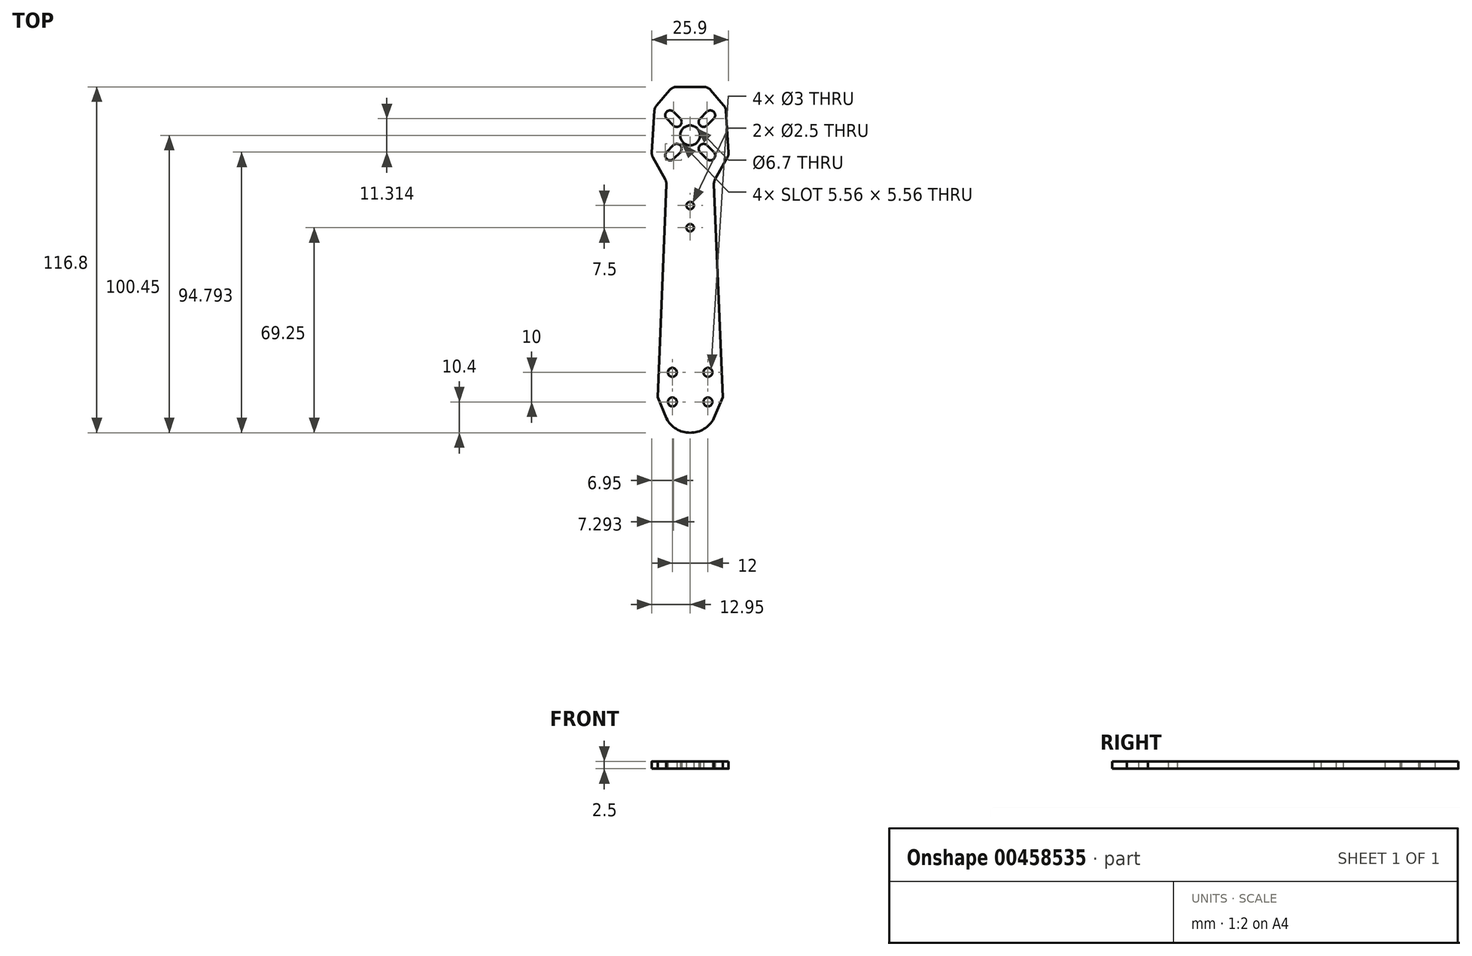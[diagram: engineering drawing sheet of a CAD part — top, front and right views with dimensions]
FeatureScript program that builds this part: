
annotation { "Feature Type Name" : "Feature", "Feature Type Description" : "" }
export const myFeature = defineFeature(function(context is Context, id is Id, definition is map)
    precondition{}
    {
        {
            var Q0;
            Q0=qCreatedBy(makeId("Top.planeOp"),FACE);
            var sketch = newSketch(context, id + "F0", { "sketchPlane" : qUnion([Q0])});
            skLineSegment(sketch, "E0", {"start": v(-11, -56) * mm, "end": v(-8.03, 15.96) * mm});
            skLineSegment(sketch, "E1", {"start": v(-8.4, 17.54) * mm, "end": v(-12.57, 25.03) * mm});
            skLineSegment(sketch, "E2", {"start": v(-12.95, 26.68) * mm, "end": v(-12.06, 40.8) * mm});
            skLineSegment(sketch, "E3", {"start": v(-11.35, 42.56) * mm, "end": v(-6.9, 47.75) * mm});
            skLineSegment(sketch, "E4", {"start": v(-4.62, 48.8) * mm, "end": v(4.62, 48.8) * mm});
            skLineSegment(sketch, "E5", {"start": v(6.9, 47.75) * mm, "end": v(11.35, 42.56) * mm});
            skLineSegment(sketch, "E6", {"start": v(12.06, 40.8) * mm, "end": v(12.95, 26.68) * mm});
            skLineSegment(sketch, "E7", {"start": v(12.57, 25.03) * mm, "end": v(8.4, 17.54) * mm});
            skLineSegment(sketch, "E8", {"start": v(8.03, 15.96) * mm, "end": v(11, -56) * mm});
            skLineSegment(sketch, "E9", {"start": v(11, -56) * mm, "end": v(8, -63.13) * mm});
            skLineSegment(sketch, "E10", {"start": v(-8, -63.13) * mm, "end": v(-11, -56) * mm});
            skPoint(sketch, "E11.visualSharp", {"position": v(0, -68) * mm});
            skArc(sketch, "E12", {"start": v(-8, -63.13) * mm, "mid": v(0, -68) * mm, "end": v(8, -63.13) * mm});
            skCircle(sketch, "E13", {"center": v(6, -47.6) * mm, "radius": 1.5 * mm});
            skCircle(sketch, "E14", {"center": v(-6, -47.6) * mm, "radius": 1.5 * mm});
            skCircle(sketch, "E15", {"center": v(6, -57.6) * mm, "radius": 1.5 * mm});
            skCircle(sketch, "E16", {"center": v(-6, -57.6) * mm, "radius": 1.5 * mm});
            skLineSegment(sketch, "E17", {"start": v(0, -68) * mm, "end": v(9.63, -68) * mm, "construction": true});
            skCircle(sketch, "E18", {"center": v(0, 1.25) * mm, "radius": 1.25 * mm});
            skCircle(sketch, "E19", {"center": v(0, 8.75) * mm, "radius": 1.25 * mm});
            skCircle(sketch, "E20", {"center": v(0, 32.45) * mm, "radius": 3.35 * mm});
            skPoint(sketch, "E20.centerSnap0", {"position": v(0, 48.8) * mm});
            skLineSegment(sketch, "E21", {"start": v(0, 32.45) * mm, "end": v(4.53, 27.92) * mm, "construction": true});
            skLineSegment(sketch, "E22", {"start": v(0, 32.45) * mm, "end": v(4.53, 36.98) * mm, "construction": true});
            skLineSegment(sketch, "E23", {"start": v(4.53, 36.98) * mm, "end": v(6.79, 39.24) * mm});
            skArc(sketch, "E24.0.startCap", {"start": v(5.7, 35.8) * mm, "mid": v(3.36, 35.8) * mm, "end": v(3.36, 38.14) * mm});
            skArc(sketch, "E24.0.endCap", {"start": v(5.62, 40.4) * mm, "mid": v(7.95, 40.4) * mm, "end": v(7.95, 38.07) * mm});
            skLineSegment(sketch, "E24.0.left", {"start": v(3.36, 38.14) * mm, "end": v(5.62, 40.4) * mm});
            skLineSegment(sketch, "E24.0.right", {"start": v(5.7, 35.8) * mm, "end": v(7.95, 38.07) * mm});
            skLineSegment(sketch, "E25.MirrorCS", {"start": v(-4.53, 36.98) * mm, "end": v(-6.79, 39.24) * mm});
            skLineSegment(sketch, "E26.MirrorCS", {"start": v(-4.53, 27.92) * mm, "end": v(-6.79, 25.66) * mm});
            skLineSegment(sketch, "E27.MirrorCS", {"start": v(4.53, 27.92) * mm, "end": v(6.79, 25.66) * mm});
            skArc(sketch, "E28.0.startCap", {"start": v(-3.36, 38.14) * mm, "mid": v(-3.36, 35.8) * mm, "end": v(-5.7, 35.8) * mm});
            skArc(sketch, "E28.0.endCap", {"start": v(-7.95, 38.07) * mm, "mid": v(-7.95, 40.4) * mm, "end": v(-5.62, 40.4) * mm});
            skLineSegment(sketch, "E28.0.left", {"start": v(-5.7, 35.8) * mm, "end": v(-7.95, 38.07) * mm});
            skLineSegment(sketch, "E28.0.right", {"start": v(-3.36, 38.14) * mm, "end": v(-5.62, 40.4) * mm});
            skArc(sketch, "E29.0.startCap", {"start": v(3.36, 26.76) * mm, "mid": v(3.36, 29.1) * mm, "end": v(5.7, 29.1) * mm});
            skArc(sketch, "E29.0.endCap", {"start": v(7.95, 26.83) * mm, "mid": v(7.95, 24.5) * mm, "end": v(5.62, 24.5) * mm});
            skLineSegment(sketch, "E29.0.left", {"start": v(5.7, 29.1) * mm, "end": v(7.95, 26.83) * mm});
            skLineSegment(sketch, "E29.0.right", {"start": v(3.36, 26.76) * mm, "end": v(5.62, 24.5) * mm});
            skArc(sketch, "E30.0.startCap", {"start": v(-5.7, 29.1) * mm, "mid": v(-3.36, 29.1) * mm, "end": v(-3.36, 26.76) * mm});
            skArc(sketch, "E30.0.endCap", {"start": v(-5.62, 24.5) * mm, "mid": v(-7.95, 24.5) * mm, "end": v(-7.95, 26.83) * mm});
            skLineSegment(sketch, "E30.0.left", {"start": v(-3.36, 26.76) * mm, "end": v(-5.62, 24.5) * mm});
            skLineSegment(sketch, "E30.0.right", {"start": v(-5.7, 29.1) * mm, "end": v(-7.95, 26.83) * mm});
            skPoint(sketch, "E31.visualSharp", {"position": v(-12, 41.8) * mm});
            skArc(sketch, "E31.filletArc", {"start": v(-11.35, 42.56) * mm, "mid": v(-11.85, 41.74) * mm, "end": v(-12.06, 40.8) * mm});
            skPoint(sketch, "E32.visualSharp", {"position": v(-6, 48.8) * mm});
            skArc(sketch, "E32.filletArc", {"start": v(-4.62, 48.8) * mm, "mid": v(-5.87, 48.53) * mm, "end": v(-6.9, 47.75) * mm});
            skPoint(sketch, "E33.visualSharp", {"position": v(6, 48.8) * mm});
            skArc(sketch, "E33.filletArc", {"start": v(6.9, 47.75) * mm, "mid": v(5.87, 48.53) * mm, "end": v(4.62, 48.8) * mm});
            skPoint(sketch, "E34.visualSharp", {"position": v(12, 41.8) * mm});
            skArc(sketch, "E34.filletArc", {"start": v(12.06, 40.8) * mm, "mid": v(11.85, 41.74) * mm, "end": v(11.35, 42.56) * mm});
            skPoint(sketch, "E35.visualSharp", {"position": v(13, 25.8) * mm});
            skArc(sketch, "E35.filletArc", {"start": v(12.57, 25.03) * mm, "mid": v(12.88, 25.83) * mm, "end": v(12.95, 26.68) * mm});
            skPoint(sketch, "E36.visualSharp", {"position": v(8, 16.8) * mm});
            skArc(sketch, "E36.filletArc", {"start": v(8.4, 17.54) * mm, "mid": v(8.11, 16.77) * mm, "end": v(8.03, 15.96) * mm});
            skPoint(sketch, "E37.visualSharp", {"position": v(-8, 16.8) * mm});
            skArc(sketch, "E37.filletArc", {"start": v(-8.03, 15.96) * mm, "mid": v(-8.11, 16.77) * mm, "end": v(-8.4, 17.54) * mm});
            skPoint(sketch, "E38.visualSharp", {"position": v(-13, 25.8) * mm});
            skArc(sketch, "E38.filletArc", {"start": v(-12.95, 26.68) * mm, "mid": v(-12.88, 25.83) * mm, "end": v(-12.57, 25.03) * mm});
            skSolve(sketch);
        }
        {
            var Q0;
            Q0=qSketchRegion(id+"F0",true);
            extrude(context, id + "F1", {"entities" : qUnion([Q0]), "depth" : 2.5 * mm});
        }
    });
